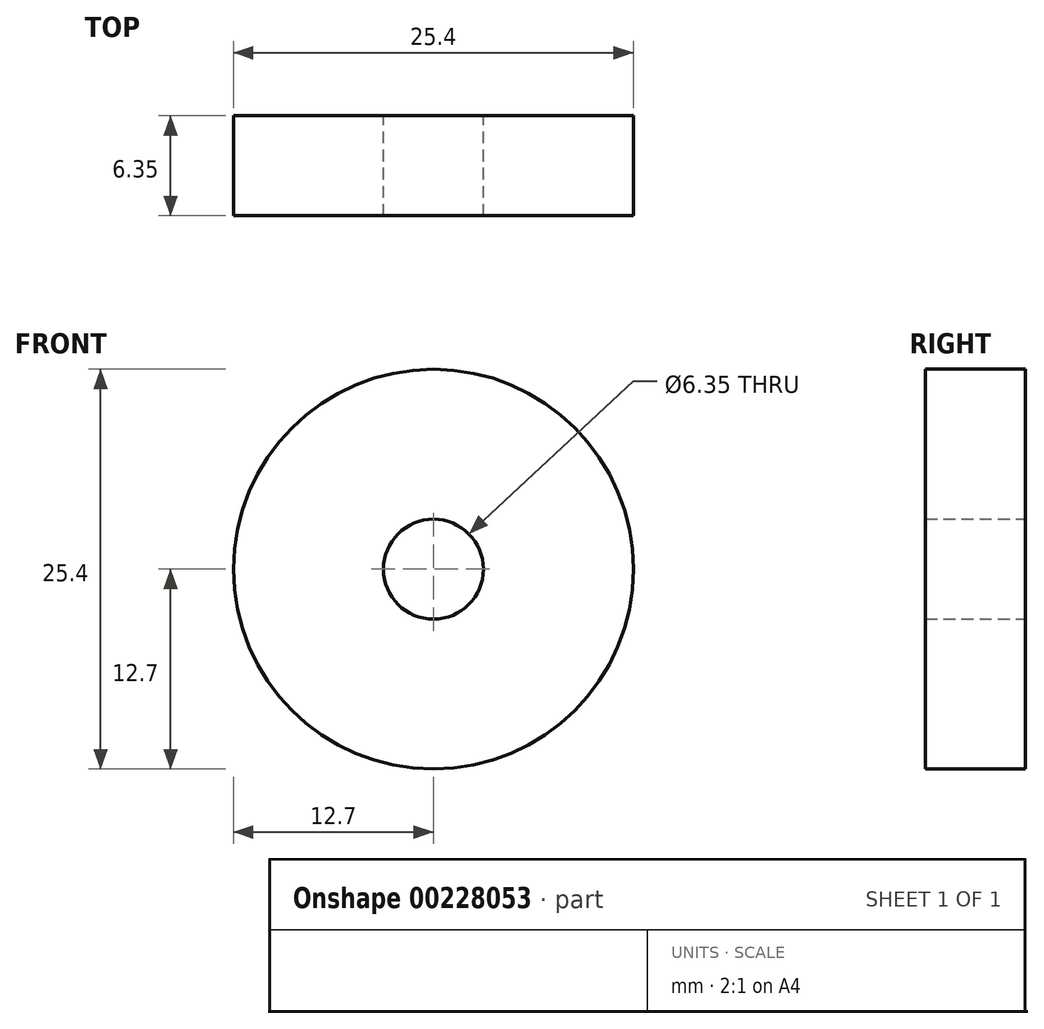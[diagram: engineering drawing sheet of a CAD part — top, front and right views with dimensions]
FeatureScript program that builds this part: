
annotation { "Feature Type Name" : "Feature", "Feature Type Description" : "" }
export const myFeature = defineFeature(function(context is Context, id is Id, definition is map)
    precondition{}
    {
        {
            var Q0;
            Q0=qCreatedBy(makeId("Front.planeOp"),FACE);
            var sketch = newSketch(context, id + "F0", { "sketchPlane" : qUnion([Q0])});
            skCircle(sketch, "E0", {"center": v(0, 0) * mm, "radius": 12.7 * mm});
            skCircle(sketch, "E1", {"center": v(0, 0) * mm, "radius": 3.18 * mm});
            skSolve(sketch);
        }
        {
            var Q0;
            Q0 = qSketchRegion(id + "F0", true);
            extrude(context, id + "F1", {"entities" : qUnion([Q0]), "depth" : 6.35 * mm, "offsetDistance" : 25.4 * mm});
        }
    });
